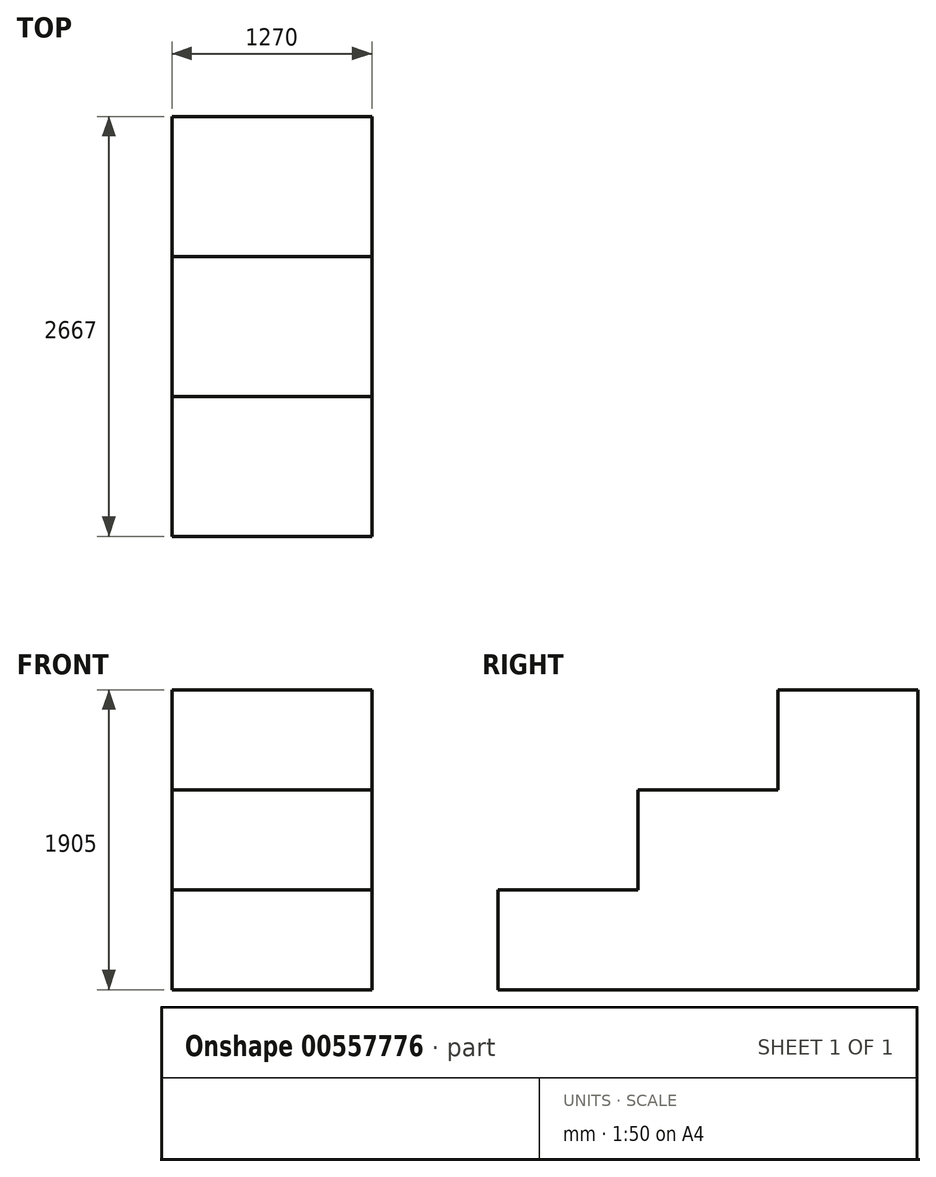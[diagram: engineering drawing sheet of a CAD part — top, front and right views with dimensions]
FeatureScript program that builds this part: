
annotation { "Feature Type Name" : "Feature", "Feature Type Description" : "" }
export const myFeature = defineFeature(function(context is Context, id is Id, definition is map)
    precondition{}
    {
        {
            var Q0;
            Q0=qCreatedBy(makeId("Right.planeOp"),FACE);
            var sketch = newSketch(context, id + "F0", { "sketchPlane" : qUnion([Q0])});
            skLineSegment(sketch, "E0", {"start": v(-68.89, 0) * mm, "end": v(-68.89, 635) * mm});
            skLineSegment(sketch, "E1", {"start": v(-68.89, 635) * mm, "end": v(820.11, 635) * mm});
            skLineSegment(sketch, "E2", {"start": v(820.11, 635) * mm, "end": v(820.11, 1270) * mm});
            skLineSegment(sketch, "E3", {"start": v(820.11, 1270) * mm, "end": v(1709.11, 1270) * mm});
            skLineSegment(sketch, "E4", {"start": v(1709.11, 1270) * mm, "end": v(1709.11, 1905) * mm});
            skLineSegment(sketch, "E5", {"start": v(1709.11, 1905) * mm, "end": v(2598.11, 1905) * mm});
            skLineSegment(sketch, "E6", {"start": v(2598.11, 1905) * mm, "end": v(2598.11, 0) * mm});
            skLineSegment(sketch, "E7", {"start": v(2598.11, 0) * mm, "end": v(-68.89, 0) * mm});
            skSolve(sketch);
        }
        {
            var Q0;
            Q0=makeQuery(id+"F0.imprint","IMPRINT",FACE,{"disambiguationData":[TD([[makeQuery(id+"F0.imprint","IMPRINT",EDGE,{"derivedFrom":sQuery(id+"F0.wireOp",EDGE,"E0")}),-1.0]])]});
            extrude(context, id + "F1", {"entities" : qUnion([Q0]), "oppositeDirection" : true, "depth" : 1270 * mm, "offsetDistance" : 25.4 * mm});
        }
    });
